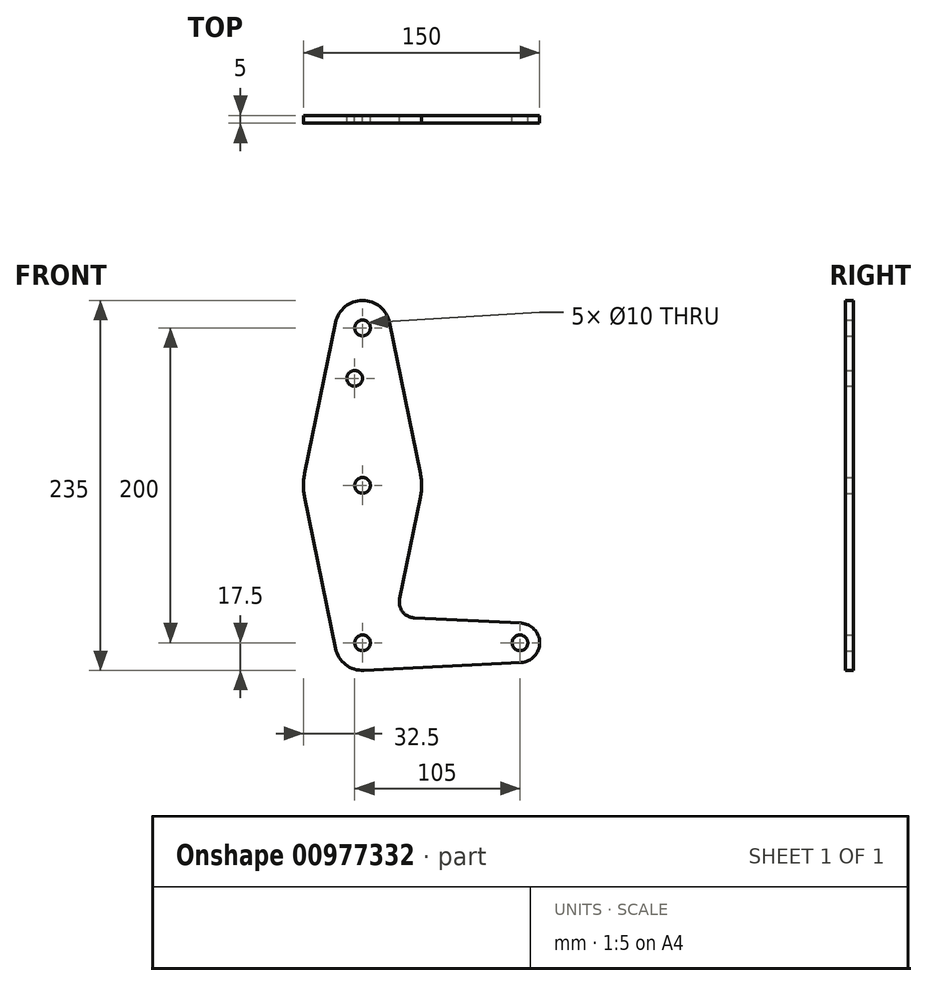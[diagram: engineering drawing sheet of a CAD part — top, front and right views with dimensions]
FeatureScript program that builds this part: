
annotation { "Feature Type Name" : "Feature", "Feature Type Description" : "" }
export const myFeature = defineFeature(function(context is Context, id is Id, definition is map)
    precondition{}
    {
        {
            var Q0;
            Q0=qCreatedBy(makeId("Front.planeOp"),FACE);
            var sketch = newSketch(context, id + "F0", { "sketchPlane" : qUnion([Q0])});
            skLineSegment(sketch, "E0", {"start": v(0, 0) * mm, "end": v(0, 200) * mm, "construction": true});
            skLineSegment(sketch, "E1", {"start": v(0, 0) * mm, "end": v(100, 0) * mm, "construction": true});
            skCircle(sketch, "E2", {"center": v(0, 200) * mm, "radius": 17.5 * mm});
            skCircle(sketch, "E3", {"center": v(0, 100) * mm, "radius": 37.5 * mm});
            skCircle(sketch, "E4", {"center": v(0, 0) * mm, "radius": 17.5 * mm});
            skCircle(sketch, "E5", {"center": v(100, 0) * mm, "radius": 12.5 * mm});
            skLineSegment(sketch, "E6", {"start": v(-36.74, 92.5) * mm, "end": v(-17.15, -3.5) * mm});
            skLineSegment(sketch, "E7", {"start": v(17.15, 203.5) * mm, "end": v(36.74, 107.5) * mm});
            skLineSegment(sketch, "E8", {"start": v(32.85, 15.88) * mm, "end": v(100.62, 12.48) * mm});
            skLineSegment(sketch, "E9", {"start": v(0.87, -17.48) * mm, "end": v(100.63, -12.48) * mm});
            skLineSegment(sketch, "E10", {"start": v(-17.15, 203.5) * mm, "end": v(-36.74, 107.5) * mm});
            skLineSegment(sketch, "E11", {"start": v(23.55, 27.87) * mm, "end": v(36.74, 92.5) * mm});
            skCircle(sketch, "E12", {"center": v(0, 200) * mm, "radius": 5 * mm});
            skCircle(sketch, "E13", {"center": v(0, 100) * mm, "radius": 5 * mm});
            skCircle(sketch, "E14", {"center": v(0, 0) * mm, "radius": 5 * mm});
            skCircle(sketch, "E15", {"center": v(-5, 168) * mm, "radius": 5 * mm});
            skCircle(sketch, "E16", {"center": v(100, 0) * mm, "radius": 5 * mm});
            skArc(sketch, "E17.filletArc", {"start": v(23.55, 27.87) * mm, "mid": v(25.45, 19.74) * mm, "end": v(32.85, 15.88) * mm});
            skSolve(sketch);
        }
        {
            var Q0;
            Q0 = qSketchRegion(id + "F0", true);
            extrude(context, id + "F1", {"entities" : qUnion([Q0]), "depth" : 5 * mm, "offsetDistance" : 25 * mm});
        }
    });
